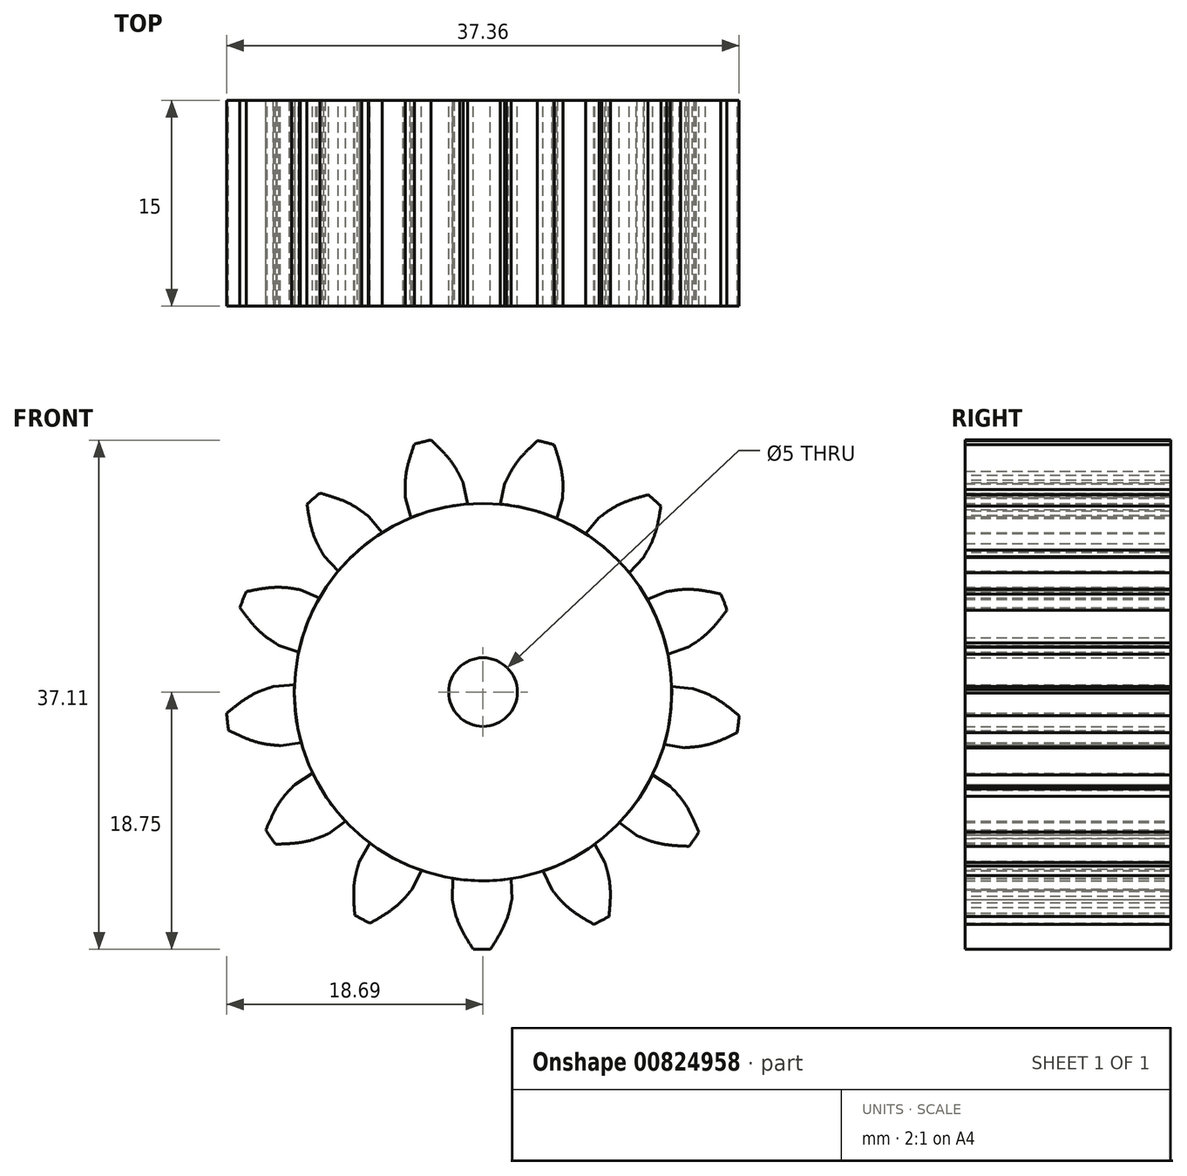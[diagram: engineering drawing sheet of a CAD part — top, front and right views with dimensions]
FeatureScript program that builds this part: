
annotation { "Feature Type Name" : "Feature", "Feature Type Description" : "" }
export const myFeature = defineFeature(function(context is Context, id is Id, definition is map)
    precondition{}
    {
        {
            var Q0;
            Q0=qCreatedBy(makeId("Front.planeOp"),FACE);
            var sketch = newSketch(context, id + "F0", { "sketchPlane" : qUnion([Q0])});
            skCircle(sketch, "E0", {"center": v(0, 0) * mm, "radius": 16.25 * mm, "construction": true});
            skCircle(sketch, "E1", {"center": v(0, 0) * mm, "radius": 18.75 * mm});
            skCircle(sketch, "E2", {"center": v(0, 0) * mm, "radius": 13.75 * mm});
            skCircle(sketch, "E3", {"center": v(0, 0) * mm, "radius": 15.27 * mm, "construction": true});
            skLineSegment(sketch, "E4", {"start": v(-3.93, 16.25) * mm, "end": v(4.33, 16.25) * mm});
            skPoint(sketch, "E5", {"position": v(0, 16.25) * mm});
            skLineSegment(sketch, "E6", {"start": v(5.22, 14.35) * mm, "end": v(-5, 18.07) * mm});
            skLineSegment(sketch, "E7", {"start": v(-5, 18.07) * mm, "end": v(0, 0) * mm, "construction": true});
            skLineSegment(sketch, "E8", {"start": v(0, 0) * mm, "end": v(5.22, 14.35) * mm, "construction": true});
            skPoint(sketch, "E9", {"position": v(-5.66, 14.18) * mm});
            skLineSegment(sketch, "E10", {"start": v(-5.66, 14.18) * mm, "end": v(0, 0) * mm, "construction": true});
            skLineSegment(sketch, "E11", {"start": v(0, 0) * mm, "end": v(2.54, 15.06) * mm, "construction": true});
            skLineSegment(sketch, "E12", {"start": v(0, 0) * mm, "end": v(-0.23, 15.27) * mm, "construction": true});
            skLineSegment(sketch, "E13", {"start": v(0, 0) * mm, "end": v(-3, 14.97) * mm, "construction": true});
            skLineSegment(sketch, "E14", {"start": v(-3, 14.97) * mm, "end": v(-5.66, 14.44) * mm});
            skLineSegment(sketch, "E15", {"start": v(-0.23, 15.27) * mm, "end": v(-5.67, 15.19) * mm});
            skLineSegment(sketch, "E16", {"start": v(2.54, 15.06) * mm, "end": v(-5.51, 16.41) * mm});
            skFitSpline(sketch, "E17", {"points": [v(-5.66, 14.18) * mm, v(-5.66, 14.44) * mm, v(-5.67, 15.19) * mm, v(-5.51, 16.41) * mm, v(-5, 18.07) * mm], "startDerivative": vector(-0.02, 1.7) * mm, "endDerivative": vector(1.68, 4.91) * mm});
            skLineSegment(sketch, "E18", {"start": v(-5.67, 15.19) * mm, "end": v(0, 0) * mm, "construction": true});
            skLineSegment(sketch, "E19", {"start": v(0, 0) * mm, "end": v(-4.4, 18.23) * mm, "construction": true});
            skLineSegment(sketch, "E20", {"start": v(-5.66, 14.18) * mm, "end": v(-5.25, 12.7) * mm});
            skFitSpline(sketch, "E21.MirrorCS", {"points": [v(-1.43, 15.2) * mm, v(-1.54, 15.43) * mm, v(-1.87, 16.1) * mm, v(-2.58, 17.12) * mm, v(-3.78, 18.36) * mm], "startDerivative": vector(-0.76, 1.51) * mm, "endDerivative": vector(-3.73, 3.6) * mm});
            skLineSegment(sketch, "E22.MirrorCS", {"start": v(-1.43, 15.2) * mm, "end": v(-1.12, 13.7) * mm});
            skSolve(sketch);
        }
        {
            var Q0;
            {var subQ0=sQuery(id+"F0.wireOp",EDGE,"E2");var subQ1=makeQuery(id+"F0.imprint","INTERSECT",VERTEX,{"derivedFrom":[subQ0,sQuery(id+"F0.wireOp",EDGE,"E20")]});Q0=makeQuery(id+"F0.imprint","IMPRINT",FACE,{"disambiguationData":[TD([[makeQuery(id+"F0.imprint","IMPRINT",EDGE,{"disambiguationData":[TD([[subQ1,1.0]])],"derivedFrom":subQ0}),1.0]])]});}
            extrude(context, id + "F1", {"entities" : qUnion([Q0]), "depth" : 15 * mm, "offsetDistance" : 25 * mm});
        }
        {
            var Q0;
            {var subQ4=sQuery(id+"F0.wireOp",EDGE,"E20");Q0=makeQuery(id+"F0.imprint","IMPRINT",FACE,{"disambiguationData":[TD([[makeQuery(id+"F0.imprint","IMPRINT",EDGE,{"derivedFrom":subQ4}),1.0]])]});}
            var Q1;
            {var subQ0=sQuery(id+"F0.wireOp",EDGE,"E17");var subQ1=sQuery(id+"F0.wireOp",EDGE,"E15");var subQ2=makeQuery(id+"F0.imprint","INTERSECT",VERTEX,{"derivedFrom":[subQ1,subQ0]});Q1=makeQuery(id+"F0.imprint","IMPRINT",FACE,{"disambiguationData":[TD([[makeQuery(id+"F0.imprint","IMPRINT",EDGE,{"disambiguationData":[TD([[subQ2,1.0]])],"derivedFrom":subQ1}),-1.0]])]});}
            var Q2;
            {var subQ0=sQuery(id+"F0.wireOp",EDGE,"E17");var subQ3=sQuery(id+"F0.wireOp",EDGE,"E16");var subQ4=makeQuery(id+"F0.imprint","INTERSECT",VERTEX,{"derivedFrom":[subQ3,subQ0]});Q2=makeQuery(id+"F0.imprint","IMPRINT",FACE,{"disambiguationData":[TD([[makeQuery(id+"F0.imprint","IMPRINT",EDGE,{"disambiguationData":[TD([[subQ4,1.0]])],"derivedFrom":subQ3}),-1.0]])]});}
            var Q3;
            {var subQ1=sQuery(id+"F0.wireOp",EDGE,"E1");var subQ3=sQuery(id+"F0.wireOp",EDGE,"E21.MirrorCS");var subQ4=makeQuery(id+"F0.imprint","INTERSECT",VERTEX,{"derivedFrom":[subQ1,subQ3]});Q3=makeQuery(id+"F0.imprint","IMPRINT",FACE,{"disambiguationData":[TD([[makeQuery(id+"F0.imprint","IMPRINT",EDGE,{"disambiguationData":[TD([[subQ4,1.0]])],"derivedFrom":subQ3}),1.0]])]});}
            extrude(context, id + "F2", {"entities" : qUnion([Q0, Q1, Q2, Q3]), "depth" : 15 * mm, "offsetDistance" : 25 * mm});
        }
        {
            var Q0;
            Q0=qCreatedBy(makeId("Right.planeOp"),FACE);
            var sketch = newSketch(context, id + "F3", { "sketchPlane" : qUnion([Q0])});
            skLineSegment(sketch, "E23", {"start": v(0, 0) * mm, "end": v(-64.7, 0) * mm});
            skSolve(sketch);
        }
        {
            var Q0;
            Q0=makeQuery(id+"F2.opExtrude","SWEPT_BODY",BODY,{"disambiguationData":[OSD([sQuery(id+"F0.wireOp",EDGE,"E1"),sQuery(id+"F0.wireOp",EDGE,"E2"),sQuery(id+"F0.wireOp",EDGE,"E17"),sQuery(id+"F0.wireOp",EDGE,"E20"),sQuery(id+"F0.wireOp",EDGE,"E21.MirrorCS"),sQuery(id+"F0.wireOp",EDGE,"E22.MirrorCS")])]});
            var Q1;
            Q1=sQuery(id+"F3.wireOp",EDGE,"E23");
            circularPattern(context, id + "F4", {"entities" : qUnion([Q0]), "axis" : qUnion([Q1]), "angle" : 360 * degree, "instanceCount" : 13, "equalSpace" : true});
        }
        {
            var Q0;
            Q0=qCreatedBy(makeId("Front.planeOp"),FACE);
            var sketch = newSketch(context, id + "F5", { "sketchPlane" : qUnion([Q0])});
            skCircle(sketch, "E24", {"center": v(0, 0) * mm, "radius": 2.5 * mm});
            skSolve(sketch);
        }
        {
            var Q0;
            Q0 = qSketchRegion(id + "F5", true);
            extrude(context, id + "F6", {"entities" : qUnion([Q0]), "operationType" : NewBodyOperationType.REMOVE, "endBound" : BoundingType.THROUGH_ALL, "depth" : 25 * mm, "offsetDistance" : 25 * mm});
        }
    });
